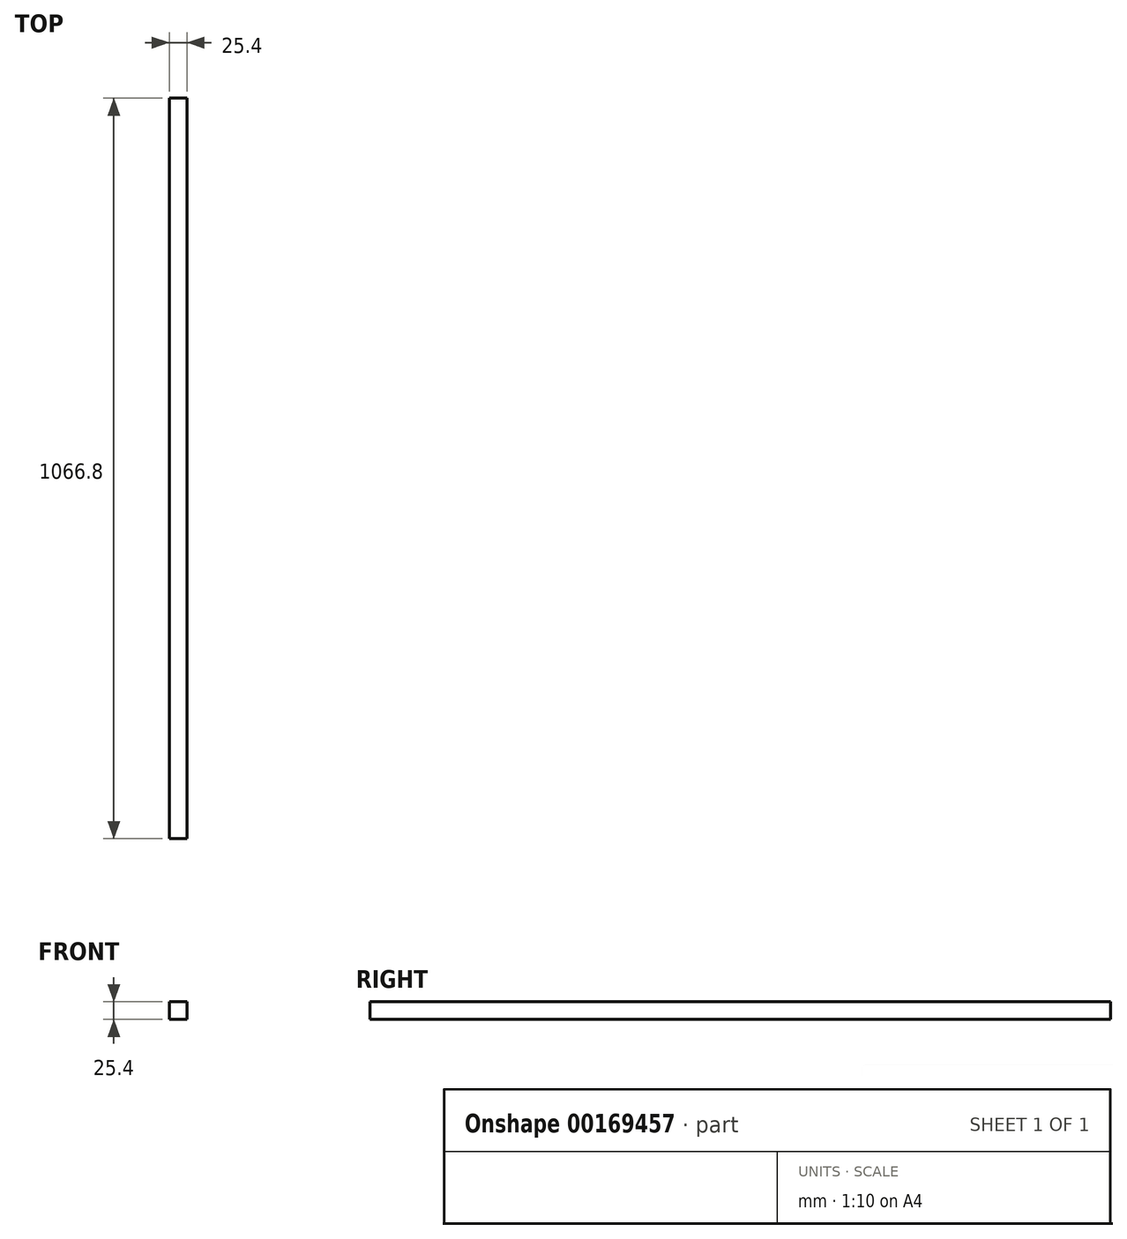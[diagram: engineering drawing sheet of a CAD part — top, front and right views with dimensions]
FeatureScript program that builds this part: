
annotation { "Feature Type Name" : "Feature", "Feature Type Description" : "" }
export const myFeature = defineFeature(function(context is Context, id is Id, definition is map)
    precondition{}
    {
        {
            var Q0;
            Q0=qCreatedBy(makeId("Front.planeOp"),FACE);
            var sketch = newSketch(context, id + "F0", { "sketchPlane" : qUnion([Q0])});
            skLineSegment(sketch, "E0.bottom", {"start": v(0, 0) * mm, "end": v(25.4, 0) * mm});
            skLineSegment(sketch, "E0.top", {"start": v(0, -25.4) * mm, "end": v(25.4, -25.4) * mm});
            skLineSegment(sketch, "E0.left", {"start": v(0, 0) * mm, "end": v(0, -25.4) * mm});
            skLineSegment(sketch, "E0.right", {"start": v(25.4, 0) * mm, "end": v(25.4, -25.4) * mm});
            skSolve(sketch);
        }
        {
            var Q0;
            Q0 = qSketchRegion(id + "F0", true);
            extrude(context, id + "F1", {"entities" : qUnion([Q0]), "depth" : 1066.8 * mm});
        }
    });
